# Revit family: 38-80-116-DN50-200
name_source: partatom
category: Pipe Accessories
units: mm (PartAtom-declared; Revit-internal decimal feet)

## family parameters
Always vertical = No
Cut with Voids When Loaded = No
Part Type = Valve - Breaks Into
Round Connector Dimension = Use Diameter
Shared = No
Work Plane-Based = No

## types (10) — shared parameters
38-063-80-163 = DN050_PN10/16
38-075-80-163 = DN065_PN10/16
38-090-80-16306499 = DN080_PN10/16
38-110-80-16306499 = DN100_PN10/16
38-125-80-16306499 = DN125_PN10/16
38-160-80-16306499 = DN150_PN10/16
38-180-80-163 = DN150_PN10/16
38-180-80-16306499 = DN150_PN10/16
38-200-80-16306499 = DN200_PN10
38-225-80-16306499 = DN200_PN10
Body_Wallthickness = 15 mm  [stored 0.0492126 ft]
Description_ = AVK GATE VALVE, FLANGED, PE PIPE ENDS
Ftc = 4 mm  [stored 0.0131234 ft]
Name_Height_reference = 10 mm  [stored 0.0328084 ft]
Rib_Height_Reference_1 = 120 mm
Rib_Height_Reference_2 = 110 mm
Rib_Height_Reference_3 = 100 mm
Rib_Thickness = 18 mm  [stored 0.0590551 ft]
Search_table = 38-80-116-DN50-200
URL product pages = https://www.avkvalves.com
zero-valued in all types: Bottom_Reference

## per-type parameters (varying)
- 38-063-80-163_DN050_PN10/16: At=45 mm  [stored 0.147638 ft]; Body_Height=101 mm; Body_depth=90 mm; Body_width=72 mm; Bonnet_Flange_Depth=118 mm; Bonnet_Flange_Width=82 mm; Bonnet_Flange_cut=8 mm  [stored 0.0262467 ft]; Bonnet_Flange_thickness=15 mm  [stored 0.0492126 ft]; Bonnet_Height=41 mm; Bonnet_Reference_height=91 mm; Bonnet_Thickness=73 mm; Bt=73 mm; Bt_2=66 mm; CL _Thickness=25 mm  [stored 0.082021 ft]; CL_Height=50 mm  [stored 0.164042 ft]; Cut_Reference=1130 mm; D=32 mm  [stored 0.104987 ft]; D1=7 mm  [stored 0.0229659 ft]; D2=29 mm  [stored 0.0951444 ft]; D_ref=34 mm  [stored 0.111549 ft]; D_ref_2=63 mm; E=11 mm  [stored 0.0360892 ft]; F1=17 mm  [stored 0.0557743 ft]; Fillet_Thickness=6 mm  [stored 0.019685 ft]; Flange_OD_2=45 mm  [stored 0.147638 ft]; Flange_OR=83 mm; Flange_Thickness=19 mm  [stored 0.062336 ft]; Flange_Thickness_cut=29 mm  [stored 0.0951444 ft]; Ftc_reference_height=83 mm; H=241 mm; H1=212 mm; H3=324 mm; Horizontal_Flange_width=166 mm; ID (Radius)=25 mm  [stored 0.082021 ft]; ID_2=20 mm  [stored 0.0656168 ft]; L=565 mm; L1=125 mm; L1_ref=105 mm; L_Dia=50 mm  [stored 0.164042 ft]; L_ref=440 mm; Name_Reference=71 mm; Name_Width=36 mm  [stored 0.11811 ft]; Neck_H=62 mm; Neck_T=23 mm  [stored 0.0754593 ft]; Neck_T2=21 mm; Nominal Diameter (DN)=50 mm  [stored 0.164042 ft]; R1tv=825 mm; R2f=15 mm  [stored 0.0492126 ft]; RF_Dia=50 mm  [stored 0.164042 ft]; Rf=277 mm; Rib_Height_Reference_4=60 mm; Rib_Width_1=36 mm  [stored 0.11811 ft]; Rib_Width_2=36 mm  [stored 0.11811 ft]; Rib_Width_3=36 mm  [stored 0.11811 ft]; Rib_depth_1=36 mm  [stored 0.11811 ft]; Rib_depth_2=36 mm  [stored 0.11811 ft]; Rib_depth_3=36 mm  [stored 0.11811 ft]; Rt=275 mm; Sleeve_L=40 mm  [stored 0.131234 ft]
- 38-075-80-163_DN065_PN10/16: At=54 mm; Body_Height=115 mm; Body_depth=107 mm; Body_width=72 mm; Bonnet_Flange_Depth=135 mm; Bonnet_Flange_Width=65 mm; Bonnet_Flange_cut=8 mm  [stored 0.0262467 ft]; Bonnet_Flange_thickness=15 mm  [stored 0.0492126 ft]; Bonnet_Height=47 mm  [stored 0.154199 ft]; Bonnet_Reference_height=105 mm; Bonnet_Thickness=73 mm; Bt=73 mm; Bt_2=66 mm; CL _Thickness=25 mm  [stored 0.082021 ft]; CL_Height=59 mm; Cut_Reference=1192 mm; D=38 mm  [stored 0.124672 ft]; D1=9 mm; D2=34 mm  [stored 0.111549 ft]; D_ref=40 mm  [stored 0.131234 ft]; D_ref_2=75 mm; E=11 mm  [stored 0.0360892 ft]; F1=20 mm  [stored 0.0656168 ft]; Fillet_Thickness=6 mm  [stored 0.019685 ft]; Flange_OD_2=51 mm; Flange_OR=93 mm; Flange_Thickness=19 mm  [stored 0.062336 ft]; Flange_Thickness_cut=30 mm  [stored 0.0984252 ft]; Ftc_reference_height=93 mm; H=271 mm; H1=237 mm; H3=364 mm; Horizontal_Flange_width=186 mm; ID (Radius)=33 mm; ID_2=28 mm; L=596 mm; L1=135 mm; L1_ref=115 mm; L_Dia=65 mm; L_ref=461 mm; Name_Reference=96 mm; Name_Width=36 mm  [stored 0.11811 ft]; Neck_H=64 mm; Neck_T=23 mm  [stored 0.0754593 ft]; Neck_T2=21 mm; Nominal Diameter (DN)=65 mm; R1tv=930 mm; R2f=15 mm  [stored 0.0492126 ft]; RF_Dia=59 mm; Rf=310 mm; Rib_Height_Reference_4=75 mm; Rib_Width_1=36 mm  [stored 0.11811 ft]; Rib_Width_2=36 mm  [stored 0.11811 ft]; Rib_Width_3=36 mm  [stored 0.11811 ft]; Rib_depth_1=36 mm  [stored 0.11811 ft]; Rib_depth_2=36 mm  [stored 0.11811 ft]; Rib_depth_3=36 mm  [stored 0.11811 ft]; Rt=310 mm; Sleeve_L=50 mm  [stored 0.164042 ft]
- 38-090-80-16306499_DN080_PN10/16: At=70 mm; Body_Height=108 mm; Body_depth=140 mm; Body_width=75 mm; Bonnet_Flange_Depth=171 mm; Bonnet_Flange_Width=76 mm; Bonnet_Flange_cut=8 mm  [stored 0.0262467 ft]; Bonnet_Flange_thickness=15 mm  [stored 0.0492126 ft]; Bonnet_Height=50 mm  [stored 0.164042 ft]; Bonnet_Reference_height=98 mm; Bonnet_Thickness=77 mm; Bt=77 mm; Bt_2=69 mm; CL _Thickness=27 mm  [stored 0.0885827 ft]; CL_Height=75 mm; Cut_Reference=1086 mm; D=45 mm  [stored 0.147638 ft]; D1=9 mm; D2=35 mm  [stored 0.114829 ft]; D_ref=47 mm  [stored 0.154199 ft]; D_ref_2=90 mm; E=15 mm  [stored 0.0492126 ft]; F1=20 mm  [stored 0.0656168 ft]; Fillet_Thickness=6 mm  [stored 0.019685 ft]; Flange_OD_2=60 mm; Flange_OR=100 mm; Flange_Thickness=19 mm  [stored 0.062336 ft]; Flange_Thickness_cut=30 mm  [stored 0.0984252 ft]; Ftc_reference_height=100 mm; H=282 mm; H1=247 mm; H3=382 mm; Horizontal_Flange_width=200 mm; ID (Radius)=40 mm  [stored 0.131234 ft]; ID_2=37 mm  [stored 0.121391 ft]; L=543 mm; L1=100 mm; L1_ref=170 mm; L_Dia=80 mm; L_ref=443 mm; Name_Reference=90 mm; Name_Width=38 mm  [stored 0.124672 ft]; Neck_H=64 mm; Neck_T=25 mm  [stored 0.082021 ft]; Neck_T2=23 mm  [stored 0.0754593 ft]; Nominal Diameter (DN)=80 mm; R1tv=1000 mm; R2f=15 mm  [stored 0.0492126 ft]; RF_Dia=66 mm; Rf=333 mm; Rib_Height_Reference_4=85 mm; Rib_Width_1=38 mm  [stored 0.124672 ft]; Rib_Width_2=38 mm  [stored 0.124672 ft]; Rib_Width_3=38 mm  [stored 0.124672 ft]; Rib_depth_1=38 mm  [stored 0.124672 ft]; Rib_depth_2=38 mm  [stored 0.124672 ft]; Rib_depth_3=38 mm  [stored 0.124672 ft]; Rt=333 mm; Sleeve_L=70 mm
- 38-110-80-16306499_DN100_PN10/16: At=83 mm; Body_Height=122 mm; Body_depth=166 mm; Body_width=80 mm; Bonnet_Flange_Depth=192 mm; Bonnet_Flange_Width=81 mm; Bonnet_Flange_cut=8 mm  [stored 0.0262467 ft]; Bonnet_Flange_thickness=15 mm  [stored 0.0492126 ft]; Bonnet_Height=55 mm; Bonnet_Reference_height=112 mm; Bonnet_Thickness=82 mm; Bt=82 mm; Bt_2=74 mm; CL _Thickness=29 mm  [stored 0.0951444 ft]; CL_Height=88 mm; Cut_Reference=1088 mm; D=55 mm; D1=10 mm  [stored 0.0328084 ft]; D2=35 mm  [stored 0.114829 ft]; D_ref=57 mm; D_ref_2=110 mm; E=15 mm  [stored 0.0492126 ft]; F1=22 mm  [stored 0.0721785 ft]; Fillet_Thickness=6 mm  [stored 0.019685 ft]; Flange_OD_2=73 mm; Flange_OR=110 mm; Flange_Thickness=19 mm  [stored 0.062336 ft]; Flange_Thickness_cut=30 mm  [stored 0.0984252 ft]; Ftc_reference_height=110 mm; H=305 mm; H1=270 mm; H3=415 mm; Horizontal_Flange_width=220 mm; ID (Radius)=50 mm  [stored 0.164042 ft]; ID_2=45 mm  [stored 0.147638 ft]; L=544 mm; L1=106 mm; L1_ref=194 mm; L_Dia=100 mm; L_ref=438 mm; Name_Reference=101 mm; Name_Width=40 mm  [stored 0.131234 ft]; Neck_H=60 mm; Neck_T=27 mm  [stored 0.0885827 ft]; Neck_T2=25 mm  [stored 0.082021 ft]; Nominal Diameter (DN)=100 mm; R1tv=1100 mm; R2f=15 mm  [stored 0.0492126 ft]; RF_Dia=78 mm; Rf=367 mm; Rib_Height_Reference_4=90 mm; Rib_Width_1=40 mm  [stored 0.131234 ft]; Rib_Width_2=40 mm  [stored 0.131234 ft]; Rib_Width_3=40 mm  [stored 0.131234 ft]; Rib_depth_1=40 mm  [stored 0.131234 ft]; Rib_depth_2=40 mm  [stored 0.131234 ft]; Rib_depth_3=40 mm  [stored 0.131234 ft]; Rt=367 mm; Sleeve_L=93 mm
- 38-125-80-16306499_DN125_PN10/16: At=97 mm; Body_Height=137 mm; Body_depth=194 mm; Body_width=90 mm; Bonnet_Flange_Depth=220 mm; Bonnet_Flange_Width=83 mm; Bonnet_Flange_cut=8 mm  [stored 0.0262467 ft]; Bonnet_Flange_thickness=15 mm  [stored 0.0492126 ft]; Bonnet_Height=63 mm; Bonnet_Reference_height=127 mm; Bonnet_Thickness=92 mm; Bt=92 mm; Bt_2=84 mm; CL _Thickness=34 mm  [stored 0.111549 ft]; CL_Height=102 mm; Cut_Reference=1094 mm; D=63 mm; D1=10 mm  [stored 0.0328084 ft]; D2=35 mm  [stored 0.114829 ft]; D_ref=65 mm; D_ref_2=125 mm; E=15 mm  [stored 0.0492126 ft]; F1=22 mm  [stored 0.0721785 ft]; Fillet_Thickness=6 mm  [stored 0.019685 ft]; Flange_OD_2=86 mm; Flange_OR=125 mm; Flange_Thickness=19 mm  [stored 0.062336 ft]; Flange_Thickness_cut=31 mm; Ftc_reference_height=125 mm; H=346 mm; H1=311 mm; H3=471 mm; Horizontal_Flange_width=250 mm; ID (Radius)=63 mm; ID_2=51 mm; L=547 mm; L1=110 mm; L1_ref=213 mm; L_Dia=125 mm; L_ref=437 mm; Name_Reference=114 mm; Name_Width=45 mm  [stored 0.147638 ft]; Neck_H=72 mm; Neck_T=32 mm  [stored 0.104987 ft]; Neck_T2=30 mm  [stored 0.0984252 ft]; Nominal Diameter (DN)=125 mm; R1tv=1250 mm; R2f=15 mm  [stored 0.0492126 ft]; RF_Dia=92 mm; Rf=417 mm; Rib_Height_Reference_4=120 mm; Rib_Width_1=45 mm  [stored 0.147638 ft]; Rib_Width_2=45 mm  [stored 0.147638 ft]; Rib_Width_3=45 mm  [stored 0.147638 ft]; Rib_depth_1=45 mm  [stored 0.147638 ft]; Rib_depth_2=45 mm  [stored 0.147638 ft]; Rib_depth_3=45 mm  [stored 0.147638 ft]; Rt=417 mm; Sleeve_L=103 mm
- 38-160-80-16306499_DN150_PN10/16: At=121 mm; Body_Height=191 mm; Body_depth=242 mm; Body_width=95 mm; Bonnet_Flange_Depth=272 mm; Bonnet_Flange_Width=116 mm; Bonnet_Flange_cut=8 mm  [stored 0.0262467 ft]; Bonnet_Flange_thickness=15 mm  [stored 0.0492126 ft]; Bonnet_Height=71 mm; Bonnet_Reference_height=181 mm; Bonnet_Thickness=97 mm; Bt=97 mm; Bt_2=89 mm; CL _Thickness=34 mm  [stored 0.111549 ft]; CL_Height=126 mm; Cut_Reference=1286 mm; D=80 mm; D1=10 mm  [stored 0.0328084 ft]; D2=34 mm  [stored 0.111549 ft]; D_ref=82 mm; D_ref_2=160 mm; E=15 mm  [stored 0.0492126 ft]; F1=22 mm  [stored 0.0721785 ft]; Fillet_Thickness=12 mm  [stored 0.0393701 ft]; Flange_OD_2=102 mm; Flange_OR=142 mm; Flange_Thickness=19 mm  [stored 0.062336 ft]; Flange_Thickness_cut=34 mm  [stored 0.111549 ft]; Ftc_reference_height=142 mm; H=400 mm; H1=366 mm; H3=543 mm; Horizontal_Flange_width=286 mm; ID (Radius)=75 mm; ID_2=65 mm; L=643 mm; L1=110 mm; L1_ref=240 mm; L_Dia=150 mm; L_ref=533 mm; Name_Reference=143 mm; Name_Width=48 mm  [stored 0.15748 ft]; Neck_H=49 mm; Neck_T=32 mm  [stored 0.104987 ft]; Neck_T2=30 mm  [stored 0.0984252 ft]; Nominal Diameter (DN)=150 mm; R1tv=1420 mm; R2f=30 mm  [stored 0.0984252 ft]; RF_Dia=106 mm; Rf=477 mm; Rib_Height_Reference_4=150 mm; Rib_Width_1=48 mm  [stored 0.15748 ft]; Rib_Width_2=48 mm  [stored 0.15748 ft]; Rib_Width_3=48 mm  [stored 0.15748 ft]; Rib_depth_1=48 mm  [stored 0.15748 ft]; Rib_depth_2=48 mm  [stored 0.15748 ft]; Rib_depth_3=48 mm  [stored 0.15748 ft]; Rt=473 mm; Sleeve_L=118 mm
- 38-180-80-163_DN150_PN10/16: At=121 mm; Body_Height=221 mm; Body_depth=242 mm; Body_width=95 mm; Bonnet_Flange_Depth=272 mm; Bonnet_Flange_Width=116 mm; Bonnet_Flange_cut=8 mm  [stored 0.0262467 ft]; Bonnet_Flange_thickness=15 mm  [stored 0.0492126 ft]; Bonnet_Height=71 mm; Bonnet_Reference_height=211 mm; Bonnet_Thickness=97 mm; Bt=97 mm; Bt_2=89 mm; CL _Thickness=34 mm  [stored 0.111549 ft]; CL_Height=126 mm; Cut_Reference=1452 mm; D=90 mm; D1=10 mm  [stored 0.0328084 ft]; D2=38 mm  [stored 0.124672 ft]; D_ref=92 mm; D_ref_2=180 mm; E=15 mm  [stored 0.0492126 ft]; F1=22 mm  [stored 0.0721785 ft]; Fillet_Thickness=12 mm  [stored 0.0393701 ft]; Flange_OD_2=108 mm; Flange_OR=142 mm; Flange_Thickness=19 mm  [stored 0.062336 ft]; Flange_Thickness_cut=33 mm; Ftc_reference_height=142 mm; H=448 mm; H1=410 mm; H3=591 mm; Horizontal_Flange_width=286 mm; ID (Radius)=75 mm; ID_2=74 mm; L=726 mm; L1=175 mm; L1_ref=175 mm; L_Dia=150 mm; L_ref=551 mm; Name_Reference=143 mm; Name_Width=48 mm  [stored 0.15748 ft]; Neck_H=63 mm; Neck_T=32 mm  [stored 0.104987 ft]; Neck_T2=30 mm  [stored 0.0984252 ft]; Nominal Diameter (DN)=150 mm; R1tv=1420 mm; R2f=30 mm  [stored 0.0984252 ft]; RF_Dia=106 mm; Rf=477 mm; Rib_Height_Reference_4=150 mm; Rib_Width_1=48 mm  [stored 0.15748 ft]; Rib_Width_2=48 mm  [stored 0.15748 ft]; Rib_Width_3=48 mm  [stored 0.15748 ft]; Rib_depth_1=48 mm  [stored 0.15748 ft]; Rib_depth_2=48 mm  [stored 0.15748 ft]; Rib_depth_3=48 mm  [stored 0.15748 ft]; Rt=473 mm; Sleeve_L=100 mm
- 38-180-80-16306499_DN150_PN10/16: At=121 mm; Body_Height=172 mm; Body_depth=242 mm; Body_width=95 mm; Bonnet_Flange_Depth=272 mm; Bonnet_Flange_Width=116 mm; Bonnet_Flange_cut=8 mm  [stored 0.0262467 ft]; Bonnet_Flange_thickness=15 mm  [stored 0.0492126 ft]; Bonnet_Height=71 mm; Bonnet_Reference_height=162 mm; Bonnet_Thickness=97 mm; Bt=97 mm; Bt_2=89 mm; CL _Thickness=34 mm  [stored 0.111549 ft]; CL_Height=126 mm; Cut_Reference=1294 mm; D=90 mm; D1=10 mm  [stored 0.0328084 ft]; D2=35 mm  [stored 0.114829 ft]; D_ref=92 mm; D_ref_2=180 mm; E=15 mm  [stored 0.0492126 ft]; F1=22 mm  [stored 0.0721785 ft]; Fillet_Thickness=12 mm  [stored 0.0393701 ft]; Flange_OD_2=108 mm; Flange_OR=142 mm; Flange_Thickness=19 mm  [stored 0.062336 ft]; Flange_Thickness_cut=33 mm; Ftc_reference_height=142 mm; H=400 mm; H1=365 mm; H3=543 mm; Horizontal_Flange_width=286 mm; ID (Radius)=75 mm; ID_2=74 mm; L=647 mm; L1=118 mm; L1_ref=232 mm; L_Dia=150 mm; L_ref=529 mm; Name_Reference=143 mm; Name_Width=48 mm  [stored 0.15748 ft]; Neck_H=67 mm; Neck_T=32 mm  [stored 0.104987 ft]; Neck_T2=30 mm  [stored 0.0984252 ft]; Nominal Diameter (DN)=150 mm; R1tv=1420 mm; R2f=30 mm  [stored 0.0984252 ft]; RF_Dia=106 mm; Rf=477 mm; Rib_Height_Reference_4=150 mm; Rib_Width_1=48 mm  [stored 0.15748 ft]; Rib_Width_2=48 mm  [stored 0.15748 ft]; Rib_Width_3=48 mm  [stored 0.15748 ft]; Rib_depth_1=48 mm  [stored 0.15748 ft]; Rib_depth_2=48 mm  [stored 0.15748 ft]; Rib_depth_3=48 mm  [stored 0.15748 ft]; Rt=473 mm; Sleeve_L=122 mm
- 38-200-80-16306499_DN200_PN10: At=147 mm; Body_Height=172 mm; Body_depth=294 mm; Body_width=95 mm; Bonnet_Flange_Depth=332 mm; Bonnet_Flange_Width=116 mm; Bonnet_Flange_cut=13 mm; Bonnet_Flange_thickness=25 mm  [stored 0.082021 ft]; Bonnet_Height=71 mm; Bonnet_Reference_height=162 mm; Bonnet_Thickness=97 mm; Bt=97 mm; Bt_2=89 mm; CL _Thickness=28 mm; CL_Height=152 mm; Cut_Reference=1294 mm; D=100 mm; D1=12 mm  [stored 0.0393701 ft]; D2=35 mm  [stored 0.114829 ft]; D_ref=102 mm; D_ref_2=200 mm; E=15 mm  [stored 0.0492126 ft]; F1=27 mm  [stored 0.0885827 ft]; Fillet_Thickness=24 mm  [stored 0.0787402 ft]; Flange_OD_2=108 mm; Flange_OR=142 mm; Flange_Thickness=19 mm  [stored 0.062336 ft]; Flange_Thickness_cut=21 mm; Ftc_reference_height=142 mm; H=400 mm; H1=365 mm; H3=543 mm; Horizontal_Flange_width=286 mm; ID (Radius)=100 mm; ID_2=74 mm; L=647 mm; L1=132 mm; L1_ref=218 mm; L_Dia=200 mm; L_ref=515 mm; Name_Reference=143 mm; Name_Width=48 mm  [stored 0.15748 ft]; Neck_H=41 mm; Neck_T=26 mm; Neck_T2=24 mm  [stored 0.0787402 ft]; Nominal Diameter (DN)=200 mm; R1tv=1420 mm; R2f=60 mm; RF_Dia=106 mm; Rf=477 mm; Rib_Height_Reference_4=150 mm; Rib_Width_1=48 mm  [stored 0.15748 ft]; Rib_Width_2=48 mm  [stored 0.15748 ft]; Rib_Width_3=48 mm  [stored 0.15748 ft]; Rib_depth_1=48 mm  [stored 0.15748 ft]; Rib_depth_2=48 mm  [stored 0.15748 ft]; Rib_depth_3=48 mm  [stored 0.15748 ft]; Rt=473 mm; Sleeve_L=122 mm
- 38-225-80-16306499_DN200_PN10: At=147 mm; Body_Height=220 mm; Body_depth=294 mm; Body_width=108 mm; Bonnet_Flange_Depth=332 mm; Bonnet_Flange_Width=132 mm; Bonnet_Flange_cut=13 mm; Bonnet_Flange_thickness=25 mm  [stored 0.082021 ft]; Bonnet_Height=85 mm; Bonnet_Reference_height=210 mm; Bonnet_Thickness=110 mm; Bt=110 mm; Bt_2=102 mm; CL _Thickness=34 mm  [stored 0.111549 ft]; CL_Height=152 mm; Cut_Reference=1342 mm; D=113 mm; D1=12 mm  [stored 0.0393701 ft]; D2=34 mm  [stored 0.111549 ft]; D_ref=115 mm; D_ref_2=225 mm; E=15 mm  [stored 0.0492126 ft]; F1=27 mm  [stored 0.0885827 ft]; Fillet_Thickness=24 mm  [stored 0.0787402 ft]; Flange_OD_2=142 mm; Flange_OR=170 mm; Flange_Thickness=20 mm  [stored 0.0656168 ft]; Flange_Thickness_cut=35 mm  [stored 0.114829 ft]; Ftc_reference_height=170 mm; H=490 mm; H1=456 mm; H3=660 mm; Horizontal_Flange_width=340 mm; ID (Radius)=100 mm; ID_2=92 mm; L=671 mm; L1=132 mm; L1_ref=295 mm; L_Dia=200 mm; L_ref=539 mm; Name_Reference=183 mm; Name_Width=54 mm; Neck_H=84 mm; Neck_T=32 mm  [stored 0.104987 ft]; Neck_T2=30 mm  [stored 0.0984252 ft]; Nominal Diameter (DN)=200 mm; R1tv=1700 mm; R2f=60 mm; RF_Dia=133 mm; Rf=567 mm; Rib_Height_Reference_4=180 mm; Rib_Width_1=54 mm; Rib_Width_2=54 mm; Rib_Width_3=54 mm; Rib_depth_1=54 mm; Rib_depth_2=54 mm; Rib_depth_3=54 mm; Rt=567 mm; Sleeve_L=160 mm

note: [stored X ft] marks values corroborated as IEEE doubles in the binary element streams (Revit-internal decimal feet)

## geometry (parser evidence)
native form markers: Extrusion x1, Sweep x3
no freeform markers — native parametric forms only
